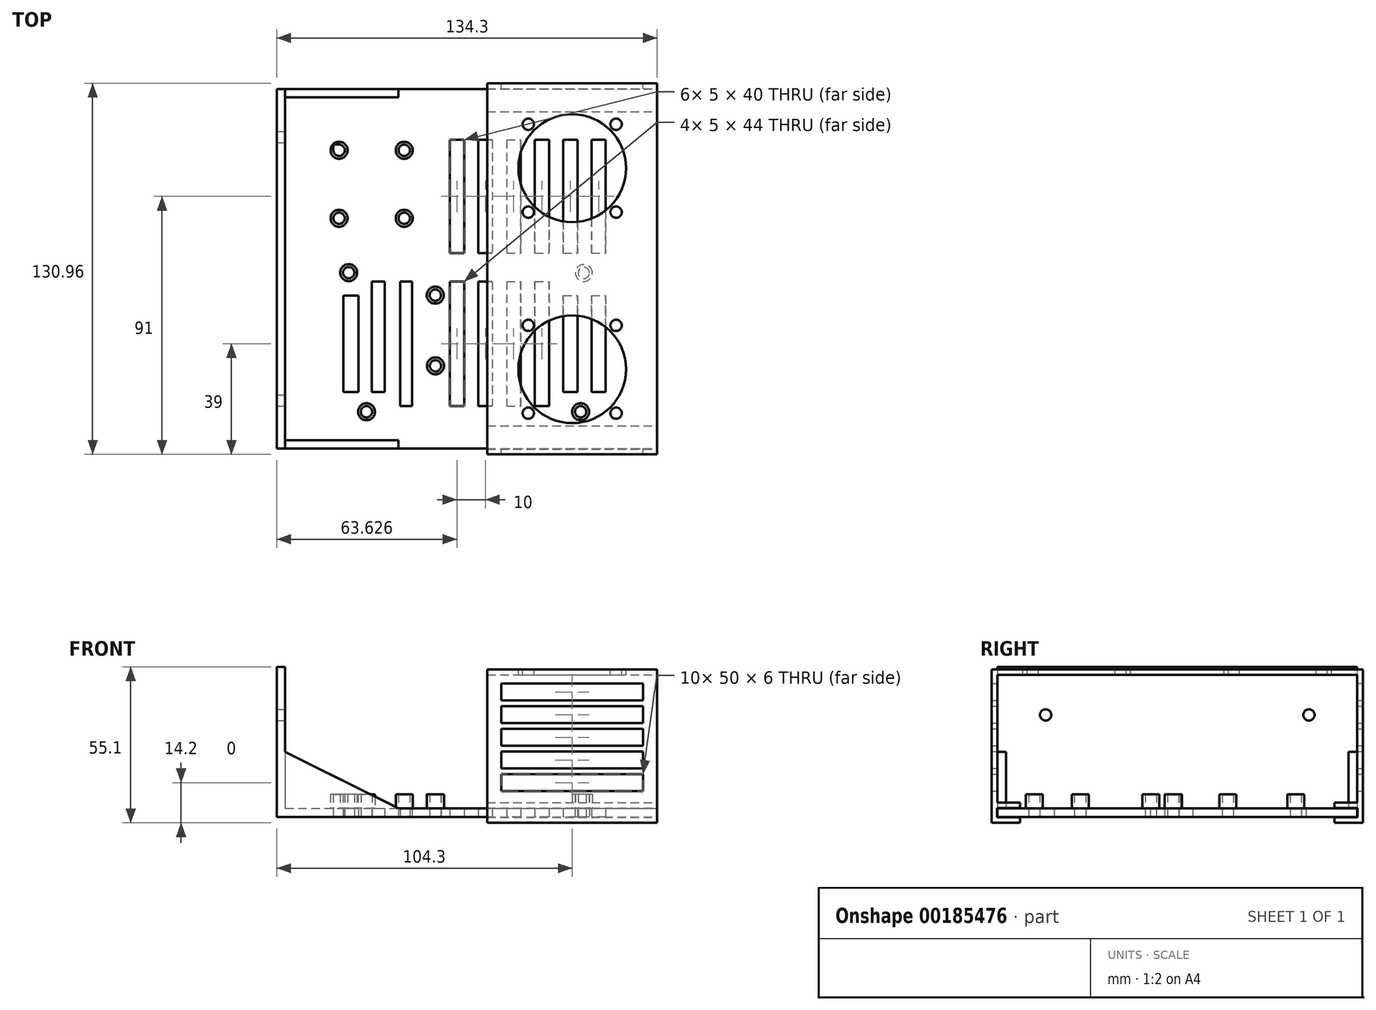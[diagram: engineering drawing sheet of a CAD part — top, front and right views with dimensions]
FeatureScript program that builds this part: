
annotation { "Feature Type Name" : "Feature", "Feature Type Description" : "" }
export const myFeature = defineFeature(function(context is Context, id is Id, definition is map)
    precondition{}
    {
        {
            var Q0;
            Q0=qCreatedBy(makeId("Top.planeOp"),FACE);
            var sketch = newSketch(context, id + "F0", { "sketchPlane" : qUnion([Q0])});
            skLineSegment(sketch, "E0.bottom", {"start": v(-46.5, 27) * mm, "end": v(48, 27) * mm});
            skLineSegment(sketch, "E0.top", {"start": v(-46.75, -27) * mm, "end": v(48, -27) * mm});
            skLineSegment(sketch, "E0.left", {"start": v(-49.5, 22.5) * mm, "end": v(-49.5, -14.5) * mm});
            skLineSegment(sketch, "E0.right", {"start": v(48, 27) * mm, "end": v(48, 23.31) * mm});
            skCircle(sketch, "E1", {"center": v(-44.1, 25.1) * mm, "radius": 2 * mm});
            skCircle(sketch, "E2", {"center": v(-37.82, -24) * mm, "radius": 2 * mm});
            skCircle(sketch, "E3", {"center": v(-13.47, -7.8) * mm, "radius": 2 * mm});
            skCircle(sketch, "E4", {"center": v(38.9, 24.99) * mm, "radius": 2 * mm});
            skCircle(sketch, "E5", {"center": v(37.78, -24) * mm, "radius": 2 * mm});
            skLineSegment(sketch, "E6.bottom", {"start": v(-49.5, -14.5) * mm, "end": v(-46.75, -14.5) * mm});
            skLineSegment(sketch, "E6.right", {"start": v(-46.75, -14.5) * mm, "end": v(-46.75, -27) * mm});
            skCircle(sketch, "E7", {"center": v(-13.52, 17.15) * mm, "radius": 2 * mm});
            skLineSegment(sketch, "E8.bottom", {"start": v(48, -17.5) * mm, "end": v(54.8, -17.5) * mm});
            skLineSegment(sketch, "E8.top", {"start": v(48, -5.37) * mm, "end": v(54.8, -5.37) * mm});
            skLineSegment(sketch, "E8.right", {"start": v(54.8, -17.5) * mm, "end": v(54.8, -5.37) * mm});
            skLineSegment(sketch, "E9.bottom", {"start": v(48, 23.31) * mm, "end": v(49.6, 23.31) * mm});
            skLineSegment(sketch, "E9.top", {"start": v(48, 14.31) * mm, "end": v(49.6, 14.31) * mm});
            skLineSegment(sketch, "E9.right", {"start": v(49.6, 23.31) * mm, "end": v(49.6, 14.31) * mm});
            skLineSegment(sketch, "E10.trimOffspring", {"start": v(48, 14.31) * mm, "end": v(48, -5.37) * mm});
            skLineSegment(sketch, "E11.trimOffspring", {"start": v(48, -17.5) * mm, "end": v(48, -27) * mm});
            skLineSegment(sketch, "E12", {"start": v(-49.5, 22.5) * mm, "end": v(-46.5, 27) * mm});
            skLineSegment(sketch, "E13.bottom", {"start": v(-69.5, -37) * mm, "end": v(64.8, -37) * mm});
            skLineSegment(sketch, "E13.top", {"start": v(-69.5, 89.96) * mm, "end": v(64.8, 89.96) * mm});
            skLineSegment(sketch, "E13.left", {"start": v(-69.5, -37) * mm, "end": v(-69.5, 89.96) * mm});
            skLineSegment(sketch, "E13.right", {"start": v(64.8, -37) * mm, "end": v(64.8, 89.96) * mm});
            skLineSegment(sketch, "E14.bottom", {"start": v(-22.25, 70.3) * mm, "end": v(-49.5, 70.3) * mm});
            skLineSegment(sketch, "E14.top", {"start": v(-22.25, 42) * mm, "end": v(-49.5, 42) * mm});
            skLineSegment(sketch, "E14.left", {"start": v(-22.25, 70.3) * mm, "end": v(-22.25, 42) * mm});
            skLineSegment(sketch, "E14.right", {"start": v(-49.5, 70.3) * mm, "end": v(-49.5, 42) * mm});
            skCircle(sketch, "E15", {"center": v(-47.5, 68.3) * mm, "radius": 2 * mm});
            skCircle(sketch, "E16", {"center": v(-24.5, 68.3) * mm, "radius": 2 * mm});
            skCircle(sketch, "E17", {"center": v(-47.5, 44.3) * mm, "radius": 2 * mm});
            skCircle(sketch, "E18", {"center": v(-24.5, 44.3) * mm, "radius": 2 * mm});
            skSolve(sketch);
        }
        {
            var Q0;
            Q0=makeQuery(id+"F0.imprint","IMPRINT",FACE,{"disambiguationData":[TD([[makeQuery(id+"F0.imprint","IMPRINT",EDGE,{"derivedFrom":sQuery(id+"F0.wireOp",EDGE,"E0.top")}),-1.0]])]});
            var Q1;
            Q1=makeQuery(id+"F0.imprint","IMPRINT",FACE,{"disambiguationData":[TD([[makeQuery(id+"F0.imprint","IMPRINT",EDGE,{"derivedFrom":sQuery(id+"F0.wireOp",EDGE,"E0.top")}),1.0]])]});
            var Q2;
            {var subQ4=sQuery(id+"F0.wireOp",EDGE,"E14.top");Q2=makeQuery(id+"F0.imprint","IMPRINT",FACE,{"disambiguationData":[TD([[makeQuery(id+"F0.imprint","IMPRINT",EDGE,{"derivedFrom":subQ4}),-1.0]])]});}
            extrude(context, id + "F1", {"entities" : qUnion([Q0, Q1, Q2]), "depth" : 3 * mm});
        }
        {
            var Q0;
            Q0=makeQuery(id+"F0.imprint","IMPRINT",FACE,{"disambiguationData":[TD([[makeQuery(id+"F0.imprint","IMPRINT",EDGE,{"derivedFrom":sQuery(id+"F0.wireOp",EDGE,"E15")}),1.0]])]});
            var Q1;
            Q1=makeQuery(id+"F0.imprint","IMPRINT",FACE,{"disambiguationData":[TD([[makeQuery(id+"F0.imprint","IMPRINT",EDGE,{"derivedFrom":sQuery(id+"F0.wireOp",EDGE,"E16")}),1.0]])]});
            var Q2;
            Q2=makeQuery(id+"F0.imprint","IMPRINT",FACE,{"disambiguationData":[TD([[makeQuery(id+"F0.imprint","IMPRINT",EDGE,{"derivedFrom":sQuery(id+"F0.wireOp",EDGE,"E17")}),1.0]])]});
            var Q3;
            Q3=makeQuery(id+"F0.imprint","IMPRINT",FACE,{"disambiguationData":[TD([[makeQuery(id+"F0.imprint","IMPRINT",EDGE,{"derivedFrom":sQuery(id+"F0.wireOp",EDGE,"E18")}),1.0]])]});
            var Q4;
            Q4=makeQuery(id+"F0.imprint","IMPRINT",FACE,{"disambiguationData":[TD([[makeQuery(id+"F0.imprint","IMPRINT",EDGE,{"derivedFrom":sQuery(id+"F0.wireOp",EDGE,"E1")}),1.0]])]});
            var Q5;
            Q5=makeQuery(id+"F0.imprint","IMPRINT",FACE,{"disambiguationData":[TD([[makeQuery(id+"F0.imprint","IMPRINT",EDGE,{"derivedFrom":sQuery(id+"F0.wireOp",EDGE,"E7")}),1.0]])]});
            var Q6;
            Q6=makeQuery(id+"F0.imprint","IMPRINT",FACE,{"disambiguationData":[TD([[makeQuery(id+"F0.imprint","IMPRINT",EDGE,{"derivedFrom":sQuery(id+"F0.wireOp",EDGE,"E4")}),1.0]])]});
            var Q7;
            Q7=makeQuery(id+"F0.imprint","IMPRINT",FACE,{"disambiguationData":[TD([[makeQuery(id+"F0.imprint","IMPRINT",EDGE,{"derivedFrom":sQuery(id+"F0.wireOp",EDGE,"E3")}),1.0]])]});
            var Q8;
            Q8=makeQuery(id+"F0.imprint","IMPRINT",FACE,{"disambiguationData":[TD([[makeQuery(id+"F0.imprint","IMPRINT",EDGE,{"derivedFrom":sQuery(id+"F0.wireOp",EDGE,"E2")}),1.0]])]});
            var Q9;
            Q9=makeQuery(id+"F0.imprint","IMPRINT",FACE,{"disambiguationData":[TD([[makeQuery(id+"F0.imprint","IMPRINT",EDGE,{"derivedFrom":sQuery(id+"F0.wireOp",EDGE,"E5")}),1.0]])]});
            extrude(context, id + "F2", {"entities" : qUnion([Q0, Q1, Q2, Q3, Q4, Q5, Q6, Q7, Q8, Q9]), "operationType" : NewBodyOperationType.REMOVE, "depth" : 25 * mm});
        }
        {
            var Q0;
            Q0=makeQuery(id+"F1.opExtrude","CAP_FACE",FACE,{"disambiguationData":[OSD([sQuery(id+"F0.wireOp",EDGE,"E1"),sQuery(id+"F0.wireOp",EDGE,"E2"),sQuery(id+"F0.wireOp",EDGE,"E3"),sQuery(id+"F0.wireOp",EDGE,"E4"),sQuery(id+"F0.wireOp",EDGE,"E5"),sQuery(id+"F0.wireOp",EDGE,"E7"),sQuery(id+"F0.wireOp",EDGE,"E13.bottom"),sQuery(id+"F0.wireOp",EDGE,"E13.top"),sQuery(id+"F0.wireOp",EDGE,"E13.left"),sQuery(id+"F0.wireOp",EDGE,"E13.right"),sQuery(id+"F0.wireOp",EDGE,"E15"),sQuery(id+"F0.wireOp",EDGE,"E16"),sQuery(id+"F0.wireOp",EDGE,"E17"),sQuery(id+"F0.wireOp",EDGE,"E18")])],"isStart":false});
            var sketch = newSketch(context, id + "F3", { "sketchPlane" : qUnion([Q0])});
            skCircle(sketch, "E19", {"center": v(-47.5, 68.3) * mm, "radius": 3 * mm});
            skCircle(sketch, "E20", {"center": v(-24.5, 68.3) * mm, "radius": 3 * mm});
            skCircle(sketch, "E21", {"center": v(-24.5, 68.3) * mm, "radius": 2 * mm});
            skCircle(sketch, "E22", {"center": v(-47.5, 68.3) * mm, "radius": 2 * mm});
            skCircle(sketch, "E23", {"center": v(-47.5, 44.3) * mm, "radius": 2 * mm});
            skCircle(sketch, "E24", {"center": v(-47.5, 44.3) * mm, "radius": 3 * mm});
            skCircle(sketch, "E25", {"center": v(-24.5, 44.3) * mm, "radius": 2 * mm});
            skCircle(sketch, "E26", {"center": v(-24.5, 44.3) * mm, "radius": 3 * mm});
            skCircle(sketch, "E27", {"center": v(-44.1, 25.1) * mm, "radius": 3 * mm});
            skCircle(sketch, "E28", {"center": v(-44.1, 25.1) * mm, "radius": 2 * mm});
            skCircle(sketch, "E29", {"center": v(-13.52, 17.15) * mm, "radius": 2 * mm});
            skCircle(sketch, "E30", {"center": v(-13.52, 17.15) * mm, "radius": 3 * mm});
            skCircle(sketch, "E31", {"center": v(38.9, 24.99) * mm, "radius": 3 * mm});
            skCircle(sketch, "E32", {"center": v(38.9, 24.99) * mm, "radius": 2 * mm});
            skCircle(sketch, "E33", {"center": v(-13.47, -7.8) * mm, "radius": 2 * mm});
            skCircle(sketch, "E34", {"center": v(-13.47, -7.8) * mm, "radius": 3 * mm});
            skCircle(sketch, "E35", {"center": v(-37.82, -24) * mm, "radius": 2 * mm});
            skCircle(sketch, "E36", {"center": v(-37.82, -24) * mm, "radius": 3 * mm});
            skCircle(sketch, "E37", {"center": v(37.78, -24) * mm, "radius": 2 * mm});
            skCircle(sketch, "E38", {"center": v(37.78, -24) * mm, "radius": 3 * mm});
            skSolve(sketch);
        }
        {
            var Q0;
            Q0=makeQuery(id+"F3.imprint","IMPRINT",FACE,{"disambiguationData":[TD([[makeQuery(id+"F3.imprint","IMPRINT",EDGE,{"derivedFrom":sQuery(id+"F3.wireOp",EDGE,"E19")}),1.0]])]});
            var Q1;
            Q1=makeQuery(id+"F3.imprint","IMPRINT",FACE,{"disambiguationData":[TD([[makeQuery(id+"F3.imprint","IMPRINT",EDGE,{"derivedFrom":sQuery(id+"F3.wireOp",EDGE,"E20")}),1.0]])]});
            var Q2;
            Q2=makeQuery(id+"F3.imprint","IMPRINT",FACE,{"disambiguationData":[TD([[makeQuery(id+"F3.imprint","IMPRINT",EDGE,{"derivedFrom":sQuery(id+"F3.wireOp",EDGE,"E25")}),-1.0]])]});
            var Q3;
            Q3=makeQuery(id+"F3.imprint","IMPRINT",FACE,{"disambiguationData":[TD([[makeQuery(id+"F3.imprint","IMPRINT",EDGE,{"derivedFrom":sQuery(id+"F3.wireOp",EDGE,"E23")}),-1.0]])]});
            var Q4;
            Q4=makeQuery(id+"F3.imprint","IMPRINT",FACE,{"disambiguationData":[TD([[makeQuery(id+"F3.imprint","IMPRINT",EDGE,{"derivedFrom":sQuery(id+"F3.wireOp",EDGE,"E27")}),1.0]])]});
            var Q5;
            Q5=makeQuery(id+"F3.imprint","IMPRINT",FACE,{"disambiguationData":[TD([[makeQuery(id+"F3.imprint","IMPRINT",EDGE,{"derivedFrom":sQuery(id+"F3.wireOp",EDGE,"E29")}),-1.0]])]});
            var Q6;
            Q6=makeQuery(id+"F3.imprint","IMPRINT",FACE,{"disambiguationData":[TD([[makeQuery(id+"F3.imprint","IMPRINT",EDGE,{"derivedFrom":sQuery(id+"F3.wireOp",EDGE,"E31")}),1.0]])]});
            var Q7;
            Q7=makeQuery(id+"F3.imprint","IMPRINT",FACE,{"disambiguationData":[TD([[makeQuery(id+"F3.imprint","IMPRINT",EDGE,{"derivedFrom":sQuery(id+"F3.wireOp",EDGE,"E33")}),-1.0]])]});
            var Q8;
            Q8=makeQuery(id+"F3.imprint","IMPRINT",FACE,{"disambiguationData":[TD([[makeQuery(id+"F3.imprint","IMPRINT",EDGE,{"derivedFrom":sQuery(id+"F3.wireOp",EDGE,"E35")}),-1.0]])]});
            var Q9;
            Q9=makeQuery(id+"F3.imprint","IMPRINT",FACE,{"disambiguationData":[TD([[makeQuery(id+"F3.imprint","IMPRINT",EDGE,{"derivedFrom":sQuery(id+"F3.wireOp",EDGE,"E37")}),-1.0]])]});
            extrude(context, id + "F4", {"entities" : qUnion([Q0, Q1, Q2, Q3, Q4, Q5, Q6, Q7, Q8, Q9]), "operationType" : NewBodyOperationType.ADD, "depth" : 5 * mm});
        }
        {
            var Q0;
            Q0=makeQuery(id+"F1.opExtrude","CAP_FACE",FACE,{"disambiguationData":[OSD([sQuery(id+"F0.wireOp",EDGE,"E1"),sQuery(id+"F0.wireOp",EDGE,"E2"),sQuery(id+"F0.wireOp",EDGE,"E3"),sQuery(id+"F0.wireOp",EDGE,"E4"),sQuery(id+"F0.wireOp",EDGE,"E5"),sQuery(id+"F0.wireOp",EDGE,"E7"),sQuery(id+"F0.wireOp",EDGE,"E13.bottom"),sQuery(id+"F0.wireOp",EDGE,"E13.top"),sQuery(id+"F0.wireOp",EDGE,"E13.left"),sQuery(id+"F0.wireOp",EDGE,"E13.right"),sQuery(id+"F0.wireOp",EDGE,"E15"),sQuery(id+"F0.wireOp",EDGE,"E16"),sQuery(id+"F0.wireOp",EDGE,"E17"),sQuery(id+"F0.wireOp",EDGE,"E18")])],"isStart":false});
            var sketch = newSketch(context, id + "F5", { "sketchPlane" : qUnion([Q0])});
            skLineSegment(sketch, "E39.bottom", {"start": v(-69.5, 89.96) * mm, "end": v(-66.5, 89.96) * mm});
            skLineSegment(sketch, "E39.top", {"start": v(-69.5, -37) * mm, "end": v(-66.5, -37) * mm});
            skLineSegment(sketch, "E39.left", {"start": v(-69.5, 89.96) * mm, "end": v(-69.5, -37) * mm});
            skLineSegment(sketch, "E39.right", {"start": v(-66.5, 89.96) * mm, "end": v(-66.5, -37) * mm});
            skSolve(sketch);
        }
        {
            var Q0;
            Q0=makeQuery(id+"F5.imprint","IMPRINT",FACE,{"disambiguationData":[TD([[makeQuery(id+"F5.imprint","IMPRINT",EDGE,{"derivedFrom":sQuery(id+"F5.wireOp",EDGE,"E39.bottom")}),-1.0]])]});
            extrude(context, id + "F6", {"entities" : qUnion([Q0]), "operationType" : NewBodyOperationType.ADD, "depth" : 50 * mm});
        }
        {
            var Q0;
            Q0=makeQuery(id+"F6.opExtrude","SWEPT_FACE",FACE,{"disambiguationData":[OSD([sQuery(id+"F5.wireOp",EDGE,"E39.right")])]});
            var sketch = newSketch(context, id + "F7", { "sketchPlane" : qUnion([Q0])});
            skCircle(sketch, "E40", {"center": v(-20, 36) * mm, "radius": 2 * mm});
            skCircle(sketch, "E41", {"center": v(72.96, 36) * mm, "radius": 2 * mm});
            skSolve(sketch);
        }
        {
            var Q0;
            Q0=makeQuery(id+"F7.imprint","IMPRINT",FACE,{"disambiguationData":[TD([[makeQuery(id+"F7.imprint","IMPRINT",EDGE,{"derivedFrom":sQuery(id+"F7.wireOp",EDGE,"E40")}),1.0]])]});
            var Q1;
            Q1=makeQuery(id+"F7.imprint","IMPRINT",FACE,{"disambiguationData":[TD([[makeQuery(id+"F7.imprint","IMPRINT",EDGE,{"derivedFrom":sQuery(id+"F7.wireOp",EDGE,"E41")}),1.0]])]});
            extrude(context, id + "F8", {"entities" : qUnion([Q0, Q1]), "operationType" : NewBodyOperationType.REMOVE, "oppositeDirection" : true, "depth" : 25 * mm});
        }
        {
            var Q0;
            Q0=makeQuery(id+"F6.boolean.opBoolean","MERGE",FACE,{"derivedFrom":[makeQuery(id+"F1.opExtrude","SWEPT_FACE",FACE,{"disambiguationData":[OSD([sQuery(id+"F0.wireOp",EDGE,"E13.bottom")])]}),makeQuery(id+"F6.opExtrude","SWEPT_FACE",FACE,{"disambiguationData":[OSD([sQuery(id+"F5.wireOp",EDGE,"E39.top")])]})]});
            var sketch = newSketch(context, id + "F9", { "sketchPlane" : qUnion([Q0])});
            skLineSegment(sketch, "E42", {"start": v(-66.5, 23) * mm, "end": v(-26.5, 3) * mm});
            skLineSegment(sketch, "E43", {"start": v(-26.5, 3) * mm, "end": v(-66.5, 3) * mm});
            skLineSegment(sketch, "E44", {"start": v(-66.5, 3) * mm, "end": v(-66.5, 23) * mm});
            skSolve(sketch);
        }
        {
            var Q0;
            Q0=makeQuery(id+"F9.imprint","IMPRINT",FACE,{"disambiguationData":[TD([[makeQuery(id+"F9.imprint","IMPRINT",EDGE,{"derivedFrom":sQuery(id+"F9.wireOp",EDGE,"E42")}),-1.0]])]});
            extrude(context, id + "F10", {"entities" : qUnion([Q0]), "operationType" : NewBodyOperationType.ADD, "oppositeDirection" : true, "depth" : 3 * mm});
        }
        {
            var Q0;
            Q0=makeQuery(id+"F6.boolean.opBoolean","MERGE",FACE,{"derivedFrom":[makeQuery(id+"F1.opExtrude","SWEPT_FACE",FACE,{"disambiguationData":[OSD([sQuery(id+"F0.wireOp",EDGE,"E13.top")])]}),makeQuery(id+"F6.opExtrude","SWEPT_FACE",FACE,{"disambiguationData":[OSD([sQuery(id+"F5.wireOp",EDGE,"E39.bottom")])]})]});
            var sketch = newSketch(context, id + "F11", { "sketchPlane" : qUnion([Q0])});
            skLineSegment(sketch, "E45", {"start": v(66.5, 23) * mm, "end": v(26.5, 3) * mm});
            skLineSegment(sketch, "E46", {"start": v(26.5, 3) * mm, "end": v(66.5, 3) * mm});
            skLineSegment(sketch, "E47", {"start": v(66.5, 3) * mm, "end": v(66.5, 23) * mm});
            skSolve(sketch);
        }
        {
            var Q0;
            Q0=makeQuery(id+"F11.imprint","IMPRINT",FACE,{"disambiguationData":[TD([[makeQuery(id+"F11.imprint","IMPRINT",EDGE,{"derivedFrom":sQuery(id+"F11.wireOp",EDGE,"E45")}),1.0]])]});
            extrude(context, id + "F12", {"entities" : qUnion([Q0]), "oppositeDirection" : true, "depth" : 3 * mm});
        }
        {
            var Q0;
            Q0=makeQuery(id+"F1.opExtrude","SWEPT_FACE",FACE,{"disambiguationData":[OSD([sQuery(id+"F0.wireOp",EDGE,"E13.right")])]});
            var sketch = newSketch(context, id + "F13", { "sketchPlane" : qUnion([Q0])});
            skLineSegment(sketch, "E48.left", {"start": v(-39, 50.1) * mm, "end": v(-39, -0.1) * mm});
            skLineSegment(sketch, "E48.right", {"start": v(-37, 50.1) * mm, "end": v(-37, 5.1) * mm});
            skLineSegment(sketch, "E49.left", {"start": v(91.96, 52.1) * mm, "end": v(91.96, 0) * mm});
            skLineSegment(sketch, "E49.right", {"start": v(89.96, 50.1) * mm, "end": v(89.96, 5.1) * mm});
            skLineSegment(sketch, "E50.bottom", {"start": v(-37, 50.1) * mm, "end": v(89.96, 50.1) * mm});
            skLineSegment(sketch, "E50.top", {"start": v(-39, 52.1) * mm, "end": v(91.96, 52.1) * mm});
            skLineSegment(sketch, "E50.left", {"start": v(-39, 50.1) * mm, "end": v(-39, 52.1) * mm});
            skLineSegment(sketch, "E50.right", {"start": v(91.96, 50.1) * mm, "end": v(91.96, 52.1) * mm});
            skLineSegment(sketch, "E51.top", {"start": v(-39, -2.1) * mm, "end": v(-29, -2.1) * mm});
            skLineSegment(sketch, "E51.left", {"start": v(-39, -0.1) * mm, "end": v(-39, -2.1) * mm});
            skLineSegment(sketch, "E52.top", {"start": v(81.96, -2.1) * mm, "end": v(91.96, -2.1) * mm});
            skLineSegment(sketch, "E53.top", {"start": v(89.96, 5.1) * mm, "end": v(81.96, 5.1) * mm});
            skPoint(sketch, "E54.orphan", {"position": v(91.96, 58.66) * mm});
            skLineSegment(sketch, "E55.trimOffspring", {"start": v(-37, 3) * mm, "end": v(-37, 0) * mm});
            skLineSegment(sketch, "E56.trimOffspring", {"start": v(89.96, 3) * mm, "end": v(89.96, 0) * mm});
            skPoint(sketch, "E57.right.end.orphan", {"position": v(-29, 5.1) * mm});
            skLineSegment(sketch, "E58", {"start": v(81.96, 5.1) * mm, "end": v(81.96, 3.1) * mm});
            skLineSegment(sketch, "E59", {"start": v(81.96, 3.1) * mm, "end": v(90.06, 3.1) * mm});
            skLineSegment(sketch, "E60", {"start": v(90.06, 3.1) * mm, "end": v(90.06, -0.1) * mm});
            skLineSegment(sketch, "E61", {"start": v(90.06, -0.1) * mm, "end": v(81.96, -0.1) * mm});
            skLineSegment(sketch, "E62", {"start": v(81.96, -0.1) * mm, "end": v(81.96, -2.1) * mm});
            skLineSegment(sketch, "E63", {"start": v(91.96, -2.1) * mm, "end": v(91.96, 0) * mm});
            skLineSegment(sketch, "E64", {"start": v(-37, 5.1) * mm, "end": v(-29, 5.1) * mm});
            skLineSegment(sketch, "E65", {"start": v(-29, 3.1) * mm, "end": v(-37.2, 3.1) * mm});
            skLineSegment(sketch, "E66", {"start": v(-37.2, 3.1) * mm, "end": v(-37.2, -0.1) * mm});
            skLineSegment(sketch, "E67", {"start": v(-37.2, -0.1) * mm, "end": v(-29, -0.1) * mm});
            skLineSegment(sketch, "E68", {"start": v(-29, -0.1) * mm, "end": v(-29, -2.1) * mm});
            skLineSegment(sketch, "E69", {"start": v(-29, 5.1) * mm, "end": v(-29, 3.1) * mm});
            skSolve(sketch);
        }
        {
            var Q0;
            Q0=makeQuery(id+"F13.imprint","IMPRINT",FACE,{"disambiguationData":[TD([[makeQuery(id+"F13.imprint","IMPRINT",EDGE,{"derivedFrom":sQuery(id+"F13.wireOp",EDGE,"E48.left")}),1.0]])]});
            var Q1;
            {var subQ0=sQuery(id+"F13.wireOp",EDGE,"E53.bottom");Q1=makeQuery(id+"F13.imprint","IMPRINT",FACE,{"disambiguationData":[TD([[makeQuery(id+"F13.imprint","IMPRINT",EDGE,{"derivedFrom":subQ0}),1.0]])]});}
            extrude(context, id + "F14", {"entities" : qUnion([Q0, Q1]), "operationType" : NewBodyOperationType.ADD, "oppositeDirection" : true, "depth" : 60 * mm});
        }
        {
            var Q0;
            Q0=makeQuery(id+"F14.opExtrude","SWEPT_FACE",FACE,{"disambiguationData":[OSD([sQuery(id+"F13.wireOp",EDGE,"E50.top")])]});
            var sketch = newSketch(context, id + "F15", { "sketchPlane" : qUnion([Q0])});
            skLineSegment(sketch, "E70.bottom", {"start": v(14.8, 81.96) * mm, "end": v(54.8, 81.96) * mm});
            skLineSegment(sketch, "E70.top", {"start": v(14.8, 41.96) * mm, "end": v(54.8, 41.96) * mm});
            skLineSegment(sketch, "E70.left", {"start": v(14.8, 81.96) * mm, "end": v(14.8, 41.96) * mm});
            skLineSegment(sketch, "E70.right", {"start": v(54.8, 81.96) * mm, "end": v(54.8, 41.96) * mm});
            skLineSegment(sketch, "E71.bottom", {"start": v(14.8, 11) * mm, "end": v(54.8, 11) * mm});
            skLineSegment(sketch, "E71.top", {"start": v(14.8, -29) * mm, "end": v(54.8, -29) * mm});
            skLineSegment(sketch, "E71.left", {"start": v(14.8, 11) * mm, "end": v(14.8, -29) * mm});
            skLineSegment(sketch, "E71.right", {"start": v(54.8, 11) * mm, "end": v(54.8, -29) * mm});
            skCircle(sketch, "E72", {"center": v(19.3, 77.46) * mm, "radius": 2 * mm});
            skCircle(sketch, "E73", {"center": v(50.3, 77.46) * mm, "radius": 2 * mm});
            skCircle(sketch, "E74", {"center": v(50.3, 46.46) * mm, "radius": 2 * mm});
            skCircle(sketch, "E75", {"center": v(19.3, 46.46) * mm, "radius": 2 * mm});
            skCircle(sketch, "E76", {"center": v(19.3, 6.5) * mm, "radius": 2 * mm});
            skCircle(sketch, "E77", {"center": v(50.3, 6.5) * mm, "radius": 2 * mm});
            skCircle(sketch, "E78", {"center": v(50.3, -24.5) * mm, "radius": 2 * mm});
            skCircle(sketch, "E79", {"center": v(19.3, -24.5) * mm, "radius": 2 * mm});
            skCircle(sketch, "E80", {"center": v(34.8, -9) * mm, "radius": 19 * mm});
            skCircle(sketch, "E81", {"center": v(34.8, 61.96) * mm, "radius": 19 * mm});
            skSolve(sketch);
        }
        {
            var Q0;
            Q0=makeQuery(id+"F15.imprint","IMPRINT",FACE,{"disambiguationData":[TD([[makeQuery(id+"F15.imprint","IMPRINT",EDGE,{"derivedFrom":sQuery(id+"F15.wireOp",EDGE,"E81")}),1.0]])]});
            var Q1;
            Q1=makeQuery(id+"F15.imprint","IMPRINT",FACE,{"disambiguationData":[TD([[makeQuery(id+"F15.imprint","IMPRINT",EDGE,{"derivedFrom":sQuery(id+"F15.wireOp",EDGE,"E72")}),1.0]])]});
            var Q2;
            Q2=makeQuery(id+"F15.imprint","IMPRINT",FACE,{"disambiguationData":[TD([[makeQuery(id+"F15.imprint","IMPRINT",EDGE,{"derivedFrom":sQuery(id+"F15.wireOp",EDGE,"E73")}),1.0]])]});
            var Q3;
            Q3=makeQuery(id+"F15.imprint","IMPRINT",FACE,{"disambiguationData":[TD([[makeQuery(id+"F15.imprint","IMPRINT",EDGE,{"derivedFrom":sQuery(id+"F15.wireOp",EDGE,"E74")}),1.0]])]});
            var Q4;
            Q4=makeQuery(id+"F15.imprint","IMPRINT",FACE,{"disambiguationData":[TD([[makeQuery(id+"F15.imprint","IMPRINT",EDGE,{"derivedFrom":sQuery(id+"F15.wireOp",EDGE,"E75")}),1.0]])]});
            var Q5;
            Q5=makeQuery(id+"F15.imprint","IMPRINT",FACE,{"disambiguationData":[TD([[makeQuery(id+"F15.imprint","IMPRINT",EDGE,{"derivedFrom":sQuery(id+"F15.wireOp",EDGE,"E76")}),1.0]])]});
            var Q6;
            Q6=makeQuery(id+"F15.imprint","IMPRINT",FACE,{"disambiguationData":[TD([[makeQuery(id+"F15.imprint","IMPRINT",EDGE,{"derivedFrom":sQuery(id+"F15.wireOp",EDGE,"E80")}),1.0]])]});
            var Q7;
            Q7=makeQuery(id+"F15.imprint","IMPRINT",FACE,{"disambiguationData":[TD([[makeQuery(id+"F15.imprint","IMPRINT",EDGE,{"derivedFrom":sQuery(id+"F15.wireOp",EDGE,"E77")}),1.0]])]});
            var Q8;
            Q8=makeQuery(id+"F15.imprint","IMPRINT",FACE,{"disambiguationData":[TD([[makeQuery(id+"F15.imprint","IMPRINT",EDGE,{"derivedFrom":sQuery(id+"F15.wireOp",EDGE,"E79")}),1.0]])]});
            var Q9;
            Q9=makeQuery(id+"F15.imprint","IMPRINT",FACE,{"disambiguationData":[TD([[makeQuery(id+"F15.imprint","IMPRINT",EDGE,{"derivedFrom":sQuery(id+"F15.wireOp",EDGE,"E78")}),1.0]])]});
            extrude(context, id + "F16", {"entities" : qUnion([Q0, Q1, Q2, Q3, Q4, Q5, Q6, Q7, Q8, Q9]), "operationType" : NewBodyOperationType.REMOVE, "oppositeDirection" : true, "depth" : 25 * mm});
        }
        {
            var Q0;
            Q0=makeQuery(id+"F14.opExtrude","SWEPT_FACE",FACE,{"disambiguationData":[OSD([sQuery(id+"F13.wireOp",EDGE,"E49.left"),sQuery(id+"F13.wireOp",EDGE,"E50.right"),sQuery(id+"F13.wireOp",EDGE,"E63")])]});
            var sketch = newSketch(context, id + "F17", { "sketchPlane" : qUnion([Q0])});
            skLineSegment(sketch, "E82.bottom", {"start": v(-59.8, 47.1) * mm, "end": v(-9.8, 47.1) * mm});
            skLineSegment(sketch, "E82.top", {"start": v(-59.8, 41.1) * mm, "end": v(-9.8, 41.1) * mm});
            skLineSegment(sketch, "E82.left", {"start": v(-59.8, 47.1) * mm, "end": v(-59.8, 41.1) * mm});
            skLineSegment(sketch, "E82.right", {"start": v(-9.8, 47.1) * mm, "end": v(-9.8, 41.1) * mm});
            skLineSegment(sketch, "E83.bottom", {"start": v(-59.8, 39.1) * mm, "end": v(-9.8, 39.1) * mm});
            skLineSegment(sketch, "E83.top", {"start": v(-59.8, 33.1) * mm, "end": v(-9.8, 33.1) * mm});
            skLineSegment(sketch, "E83.left", {"start": v(-59.8, 39.1) * mm, "end": v(-59.8, 33.1) * mm});
            skLineSegment(sketch, "E83.right", {"start": v(-9.8, 39.1) * mm, "end": v(-9.8, 33.1) * mm});
            skLineSegment(sketch, "E84.bottom", {"start": v(-59.8, 31.1) * mm, "end": v(-9.8, 31.1) * mm});
            skLineSegment(sketch, "E84.top", {"start": v(-59.8, 25.1) * mm, "end": v(-9.8, 25.1) * mm});
            skLineSegment(sketch, "E84.left", {"start": v(-59.8, 31.1) * mm, "end": v(-59.8, 25.1) * mm});
            skLineSegment(sketch, "E84.right", {"start": v(-9.8, 31.1) * mm, "end": v(-9.8, 25.1) * mm});
            skLineSegment(sketch, "E85.bottom", {"start": v(-59.8, 23.1) * mm, "end": v(-9.8, 23.1) * mm});
            skLineSegment(sketch, "E85.top", {"start": v(-59.8, 17.1) * mm, "end": v(-9.8, 17.1) * mm});
            skLineSegment(sketch, "E85.left", {"start": v(-59.8, 23.1) * mm, "end": v(-59.8, 17.1) * mm});
            skLineSegment(sketch, "E85.right", {"start": v(-9.8, 23.1) * mm, "end": v(-9.8, 17.1) * mm});
            skLineSegment(sketch, "E86.bottom", {"start": v(-59.8, 15.1) * mm, "end": v(-9.8, 15.1) * mm});
            skLineSegment(sketch, "E86.top", {"start": v(-59.8, 9.1) * mm, "end": v(-9.8, 9.1) * mm});
            skLineSegment(sketch, "E86.left", {"start": v(-59.8, 15.1) * mm, "end": v(-59.8, 9.1) * mm});
            skLineSegment(sketch, "E86.right", {"start": v(-9.8, 15.1) * mm, "end": v(-9.8, 9.1) * mm});
            skSolve(sketch);
        }
        {
            var Q0;
            Q0=makeQuery(id+"F17.imprint","IMPRINT",FACE,{"disambiguationData":[TD([[makeQuery(id+"F17.imprint","IMPRINT",EDGE,{"derivedFrom":sQuery(id+"F17.wireOp",EDGE,"E82.bottom")}),-1.0]])]});
            var Q1;
            Q1=makeQuery(id+"F17.imprint","IMPRINT",FACE,{"disambiguationData":[TD([[makeQuery(id+"F17.imprint","IMPRINT",EDGE,{"derivedFrom":sQuery(id+"F17.wireOp",EDGE,"E83.bottom")}),-1.0]])]});
            var Q2;
            Q2=makeQuery(id+"F17.imprint","IMPRINT",FACE,{"disambiguationData":[TD([[makeQuery(id+"F17.imprint","IMPRINT",EDGE,{"derivedFrom":sQuery(id+"F17.wireOp",EDGE,"E84.bottom")}),-1.0]])]});
            var Q3;
            Q3=makeQuery(id+"F17.imprint","IMPRINT",FACE,{"disambiguationData":[TD([[makeQuery(id+"F17.imprint","IMPRINT",EDGE,{"derivedFrom":sQuery(id+"F17.wireOp",EDGE,"E85.bottom")}),-1.0]])]});
            var Q4;
            Q4=makeQuery(id+"F17.imprint","IMPRINT",FACE,{"disambiguationData":[TD([[makeQuery(id+"F17.imprint","IMPRINT",EDGE,{"derivedFrom":sQuery(id+"F17.wireOp",EDGE,"E86.bottom")}),-1.0]])]});
            extrude(context, id + "F18", {"entities" : qUnion([Q0, Q1, Q2, Q3, Q4]), "operationType" : NewBodyOperationType.REMOVE, "oppositeDirection" : true, "depth" : 200 * mm});
        }
        {
            var Q0;
            Q0=makeQuery(id+"F0.imprint","IMPRINT",FACE,{"disambiguationData":[TD([[makeQuery(id+"F0.imprint","IMPRINT",EDGE,{"derivedFrom":sQuery(id+"F0.wireOp",EDGE,"E0.bottom")}),1.0]])]});
            var sketch = newSketch(context, id + "F19", { "sketchPlane" : qUnion([Q0])});
            skLineSegment(sketch, "E87.bottom", {"start": v(46.63, -17) * mm, "end": v(41.63, -17) * mm});
            skLineSegment(sketch, "E87.top", {"start": v(46.63, 17) * mm, "end": v(41.63, 17) * mm});
            skLineSegment(sketch, "E87.left", {"start": v(46.63, -17) * mm, "end": v(46.63, 17) * mm});
            skLineSegment(sketch, "E87.right", {"start": v(41.63, -17) * mm, "end": v(41.63, 17) * mm});
            skLineSegment(sketch, "E88.bottom", {"start": v(26.63, -22) * mm, "end": v(21.63, -22) * mm});
            skLineSegment(sketch, "E88.top", {"start": v(26.63, 22) * mm, "end": v(21.63, 22) * mm});
            skLineSegment(sketch, "E88.left", {"start": v(26.63, -22) * mm, "end": v(26.63, 22) * mm});
            skLineSegment(sketch, "E88.right", {"start": v(21.63, -22) * mm, "end": v(21.63, 22) * mm});
            skLineSegment(sketch, "E89.bottom", {"start": v(16.63, -22) * mm, "end": v(11.63, -22) * mm});
            skLineSegment(sketch, "E89.top", {"start": v(16.63, 22) * mm, "end": v(11.63, 22) * mm});
            skLineSegment(sketch, "E89.left", {"start": v(16.63, -22) * mm, "end": v(16.63, 22) * mm});
            skLineSegment(sketch, "E89.right", {"start": v(11.63, -22) * mm, "end": v(11.63, 22) * mm});
            skLineSegment(sketch, "E90.bottom", {"start": v(6.63, -22) * mm, "end": v(1.63, -22) * mm});
            skLineSegment(sketch, "E90.top", {"start": v(6.63, 22) * mm, "end": v(1.63, 22) * mm});
            skLineSegment(sketch, "E90.left", {"start": v(6.63, -22) * mm, "end": v(6.63, 22) * mm});
            skLineSegment(sketch, "E90.right", {"start": v(1.63, -22) * mm, "end": v(1.63, 22) * mm});
            skLineSegment(sketch, "E91.bottom", {"start": v(-3.37, -22) * mm, "end": v(-8.37, -22) * mm});
            skLineSegment(sketch, "E91.top", {"start": v(-3.37, 22) * mm, "end": v(-8.37, 22) * mm});
            skLineSegment(sketch, "E91.left", {"start": v(-8.37, -22) * mm, "end": v(-8.37, 22) * mm});
            skLineSegment(sketch, "E91.right", {"start": v(-3.37, -22) * mm, "end": v(-3.37, 22) * mm});
            skLineSegment(sketch, "E92.bottom", {"start": v(-21.75, -22) * mm, "end": v(-25.92, -22) * mm});
            skLineSegment(sketch, "E92.top", {"start": v(-21.75, 22) * mm, "end": v(-25.92, 22) * mm});
            skLineSegment(sketch, "E92.left", {"start": v(-21.75, -22) * mm, "end": v(-21.75, 22) * mm});
            skLineSegment(sketch, "E92.right", {"start": v(-25.92, -22) * mm, "end": v(-25.92, 22) * mm});
            skLineSegment(sketch, "E93.bottom", {"start": v(-31.32, -17) * mm, "end": v(-35.99, -17) * mm});
            skLineSegment(sketch, "E93.top", {"start": v(-31.32, 22) * mm, "end": v(-35.99, 22) * mm});
            skLineSegment(sketch, "E93.left", {"start": v(-31.32, -17) * mm, "end": v(-31.32, 22) * mm});
            skLineSegment(sketch, "E93.right", {"start": v(-35.99, -17) * mm, "end": v(-35.99, 22) * mm});
            skLineSegment(sketch, "E94.bottom", {"start": v(-40.65, -17) * mm, "end": v(-46.05, -17) * mm});
            skLineSegment(sketch, "E94.top", {"start": v(-40.65, 17) * mm, "end": v(-46.05, 17) * mm});
            skLineSegment(sketch, "E94.left", {"start": v(-40.65, -17) * mm, "end": v(-40.65, 17) * mm});
            skLineSegment(sketch, "E94.right", {"start": v(-46.05, -17) * mm, "end": v(-46.05, 17) * mm});
            skLineSegment(sketch, "E95.bottom", {"start": v(46.63, 32) * mm, "end": v(41.63, 32) * mm});
            skLineSegment(sketch, "E95.top", {"start": v(46.63, 72) * mm, "end": v(41.63, 72) * mm});
            skLineSegment(sketch, "E95.left", {"start": v(46.63, 32) * mm, "end": v(46.63, 72) * mm});
            skLineSegment(sketch, "E95.right", {"start": v(41.63, 32) * mm, "end": v(41.63, 72) * mm});
            skLineSegment(sketch, "E96.bottom", {"start": v(26.63, 32) * mm, "end": v(21.63, 32) * mm});
            skLineSegment(sketch, "E96.top", {"start": v(26.63, 72) * mm, "end": v(21.63, 72) * mm});
            skLineSegment(sketch, "E96.left", {"start": v(26.63, 32) * mm, "end": v(26.63, 72) * mm});
            skLineSegment(sketch, "E96.right", {"start": v(21.63, 32) * mm, "end": v(21.63, 72) * mm});
            skLineSegment(sketch, "E97.bottom", {"start": v(16.63, 32) * mm, "end": v(11.63, 32) * mm});
            skLineSegment(sketch, "E97.top", {"start": v(16.63, 72) * mm, "end": v(11.63, 72) * mm});
            skLineSegment(sketch, "E97.left", {"start": v(16.63, 32) * mm, "end": v(16.63, 72) * mm});
            skLineSegment(sketch, "E97.right", {"start": v(11.63, 32) * mm, "end": v(11.63, 72) * mm});
            skLineSegment(sketch, "E98.bottom", {"start": v(6.63, 32) * mm, "end": v(1.63, 32) * mm});
            skLineSegment(sketch, "E98.top", {"start": v(6.63, 72) * mm, "end": v(1.63, 72) * mm});
            skLineSegment(sketch, "E98.left", {"start": v(6.63, 32) * mm, "end": v(6.63, 72) * mm});
            skLineSegment(sketch, "E98.right", {"start": v(1.63, 32) * mm, "end": v(1.63, 72) * mm});
            skLineSegment(sketch, "E99.bottom", {"start": v(-3.37, 32) * mm, "end": v(-8.37, 32) * mm});
            skLineSegment(sketch, "E99.top", {"start": v(-3.37, 72) * mm, "end": v(-8.37, 72) * mm});
            skLineSegment(sketch, "E99.left", {"start": v(-8.37, 32) * mm, "end": v(-8.37, 72) * mm});
            skLineSegment(sketch, "E99.right", {"start": v(-3.37, 32) * mm, "end": v(-3.37, 72) * mm});
            skLineSegment(sketch, "E100.bottom", {"start": v(36.63, 32) * mm, "end": v(31.63, 32) * mm});
            skLineSegment(sketch, "E100.top", {"start": v(36.63, 72) * mm, "end": v(31.63, 72) * mm});
            skLineSegment(sketch, "E100.left", {"start": v(36.63, 32) * mm, "end": v(36.63, 72) * mm});
            skLineSegment(sketch, "E100.right", {"start": v(31.63, 32) * mm, "end": v(31.63, 72) * mm});
            skPoint(sketch, "E101.right.end.orphan", {"position": v(31.63, 17) * mm});
            skLineSegment(sketch, "E102.bottom", {"start": v(36.63, -17) * mm, "end": v(31.63, -17) * mm});
            skLineSegment(sketch, "E102.top", {"start": v(36.63, 17) * mm, "end": v(31.63, 17) * mm});
            skLineSegment(sketch, "E102.left", {"start": v(36.63, -17) * mm, "end": v(36.63, 17) * mm});
            skLineSegment(sketch, "E102.right", {"start": v(31.63, -17) * mm, "end": v(31.63, 17) * mm});
            skSolve(sketch);
        }
        {
            var Q0;
            Q0 = qSketchRegion(id + "F19", true);
            extrude(context, id + "F20", {"entities" : qUnion([Q0]), "operationType" : NewBodyOperationType.REMOVE, "depth" : 25 * mm});
        }
    });
